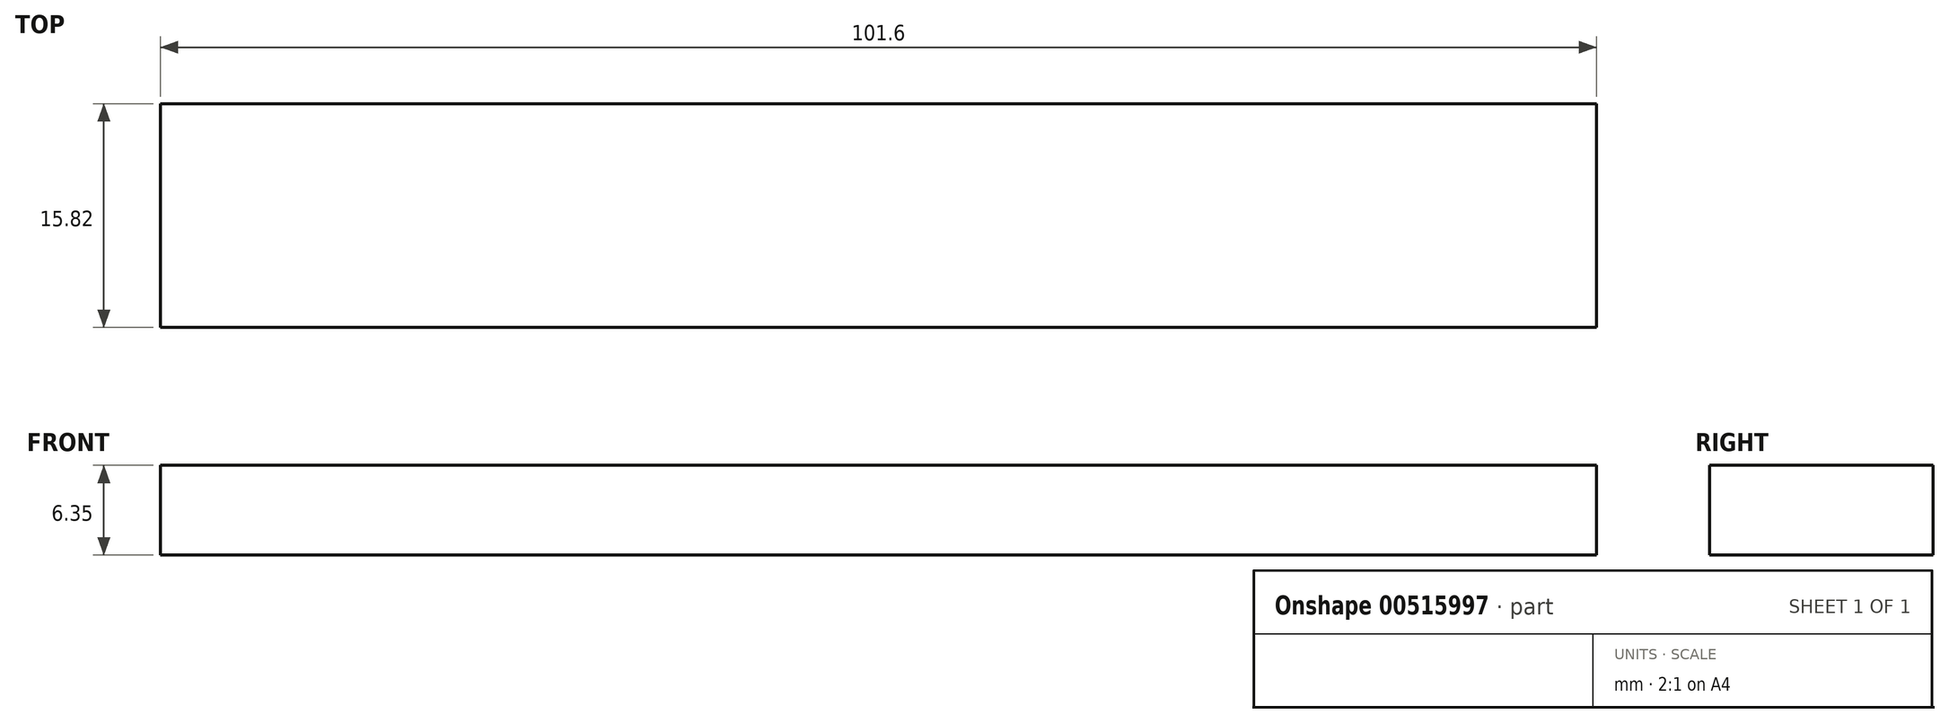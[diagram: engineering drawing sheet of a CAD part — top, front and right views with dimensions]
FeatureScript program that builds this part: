
annotation { "Feature Type Name" : "Feature", "Feature Type Description" : "" }
export const myFeature = defineFeature(function(context is Context, id is Id, definition is map)
    precondition{}
    {
        {
            var Q0;
            Q0=qCreatedBy(makeId("Top.planeOp"),FACE);
            var sketch = newSketch(context, id + "F0", { "sketchPlane" : qUnion([Q0])});
            skLineSegment(sketch, "E0.bottom", {"start": v(50.8, 7.91) * mm, "end": v(-50.8, 7.91) * mm});
            skLineSegment(sketch, "E0.top", {"start": v(50.8, -7.91) * mm, "end": v(-50.8, -7.91) * mm});
            skLineSegment(sketch, "E0.left", {"start": v(50.8, 7.91) * mm, "end": v(50.8, -7.91) * mm});
            skLineSegment(sketch, "E0.right", {"start": v(-50.8, 7.91) * mm, "end": v(-50.8, -7.91) * mm});
            skPoint(sketch, "E0.middle", {"position": v(0, 0) * mm});
            skSolve(sketch);
        }
        {
            var Q0;
            Q0=makeQuery(id+"F0.imprint","IMPRINT",FACE,{"disambiguationData":[TD([[makeQuery(id+"F0.imprint","IMPRINT",EDGE,{"derivedFrom":sQuery(id+"F0.wireOp",EDGE,"E0.bottom")}),1.0]])]});
            extrude(context, id + "F1", {"entities" : qUnion([Q0]), "depth" : 6.35 * mm, "offsetDistance" : 25.4 * mm});
        }
    });
